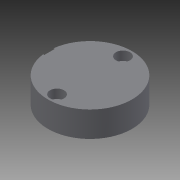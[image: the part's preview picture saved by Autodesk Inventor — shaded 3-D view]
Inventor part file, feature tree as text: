
AUTODESK INVENTOR PART (.ipt)
format: ipt  version: 2014 (Build 180170000, 170)  size: 220,160 bytes
history: native  units: in
note: dims shown in document units (in); Inventor stores cm internally (conversion verified against a paired STEP export)
features: other x189, sketch x9, hole x7, revolve x2, thread x1
ambient origin geometry x8: Origin, YZ Plane, XZ Plane, XY Plane, X Axis, Y Axis, Z Axis, Center Point
bodies: Solid1 (feature_tree)
feature tree (208):
  revolve  "Revolution1"  Angle=360.0deg
  revolve  "Revolution2"  [1 undecoded]
  thread  "Thread1"  [1 undecoded]
  hole  "Hole1"  [1 undecoded]
  hole  "Hole2"  [1 undecoded]
  hole  "Hole3"  [1 undecoded]
  hole  "Hole4"  [1 undecoded]
  hole  "Hole5"  [1 undecoded]
  hole  "Hole6"  [1 undecoded]
  hole  "Hole7"  [1 undecoded]
  other  "a1_XY"
  other  "a1_YZ"
  other  "a1_ZX"
  other  "a1_X"
  other  "a1_Y"
  other  "a1_Z"
  other  "a1_Center"
  other  "a2_XY"
  other  "a2_YZ"
  other  "a2_ZX"
  other  "a2_X"
  other  "a2_Y"
  other  "a2_Z"
  other  "a2_Center"
  other  "ar3_XY"
  other  "ar3_YZ"
  other  "ar3_ZX"
  other  "ar3_X"
  other  "ar3_Y"
  other  "ar3_Z"
  other  "ar3_Center"
  other  "ar4_XY"
  other  "ar4_YZ"
  other  "ar4_ZX"
  other  "ar4_X"
  other  "ar4_Y"
  other  "ar4_Z"
  other  "ar4_Center"
  other  "ar5_XY"
  other  "ar5_YZ"
  other  "ar5_ZX"
  other  "ar5_X"
  other  "ar5_Y"
  other  "ar5_Z"
  other  "ar5_Center"
  other  "ar6_XY"
  other  "ar6_YZ"
  other  "ar6_ZX"
  other  "ar6_X"
  other  "ar6_Y"
  other  "ar6_Z"
  other  "ar6_Center"
  other  "b1_XY"
  other  "b1_YZ"
  other  "b1_ZX"
  other  "b1_X"
  other  "b1_Y"
  other  "b1_Z"
  other  "b1_Center"
  other  "c1_XY"
  other  "c1_YZ"
  other  "c1_ZX"
  other  "c1_X"
  other  "c1_Y"
  other  "c1_Z"
  other  "c1_Center"
  other  "c2_XY"
  other  "c2_YZ"
  other  "c2_ZX"
  other  "c2_X"
  other  "c2_Y"
  other  "c2_Z"
  other  "c2_Center"
  other  "d1_XY"
  other  "d1_YZ"
  other  "d1_ZX"
  other  "d1_X"
  other  "d1_Y"
  other  "d1_Z"
  other  "d1_Center"
  other  "d2_XY"
  other  "d2_YZ"
  other  "d2_ZX"
  other  "d2_X"
  other  "d2_Y"
  other  "d2_Z"
  other  "d2_Center"
  other  "j_XY"
  other  "j_YZ"
  other  "j_ZX"
  other  "j_X"
  other  "j_Y"
  other  "j_Z"
  other  "j_Center"
  other  "k1_XY"
  other  "k1_YZ"
  other  "k1_ZX"
  other  "k1_X"
  other  "k1_Y"
  other  "k1_Z"
  other  "k1_Center"
  other  "k2_XY"
  other  "k2_YZ"
  other  "k2_ZX"
  other  "k2_X"
  other  "k2_Y"
  other  "k2_Z"
  other  "k2_Center"
  other  "l1_XY"
  other  "l1_YZ"
  other  "l1_ZX"
  other  "l1_X"
  other  "l1_Y"
  other  "l1_Z"
  other  "l1_Center"
  other  "l2_XY"
  other  "l2_YZ"
  other  "l2_ZX"
  other  "l2_X"
  other  "l2_Y"
  other  "l2_Z"
  other  "l2_Center"
  other  "rg_XY"
  other  "rg_YZ"
  other  "rg_ZX"
  other  "rg_X"
  other  "rg_Y"
  other  "rg_Z"
  other  "rg_Center"
  other  "rh_XY"
  other  "rh_YZ"
  other  "rh_ZX"
  other  "rh_X"
  other  "rh_Y"
  other  "rh_Z"
  other  "rh_Center"
  other  "to_dummy_XY"
  other  "to_dummy_YZ"
  other  "to_dummy_ZX"
  other  "to_dummy_X"
  other  "to_dummy_Y"
  other  "to_dummy_Z"
  other  "to_dummy_Center"
  other  "to_nut_XY"
  other  "to_nut_YZ"
  other  "to_nut_ZX"
  other  "to_nut_X"
  other  "to_nut_Y"
  other  "to_nut_Z"
  other  "to_nut_Center"
  other  "to_rod_XY"
  other  "to_rod_YZ"
  other  "to_rod_ZX"
  other  "to_rod_X"
  other  "to_rod_Y"
  other  "to_rod_Z"
  other  "to_rod_Center"
  other  "to_tube_XY"
  other  "to_tube_YZ"
  other  "to_tube_ZX"
  other  "to_tube_X"
  other  "to_tube_Y"
  other  "to_tube_Z"
  other  "to_tube_Center"
  other  "to_wiper_XY"
  other  "to_wiper_YZ"
  other  "to_wiper_ZX"
  other  "to_wiper_X"
  other  "to_wiper_Y"
  other  "to_wiper_Z"
  other  "to_wiper_Center"
  other  "track1_XY"
  other  "track1_YZ"
  other  "track1_ZX"
  other  "track1_X"
  other  "track1_Y"
  other  "track1_Z"
  other  "track1_Center"
  other  "track2_XY"
  other  "track2_YZ"
  other  "track2_ZX"
  other  "track2_X"
  other  "track2_Y"
  other  "track2_Z"
  other  "track2_Center"
  other  "track3_XY"
  other  "track3_YZ"
  other  "track3_ZX"
  other  "track3_X"
  other  "track3_Y"
  other  "track3_Z"
  other  "track3_Center"
  other  "track4_XY"
  other  "track4_YZ"
  other  "track4_ZX"
  other  "track4_X"
  other  "track4_Y"
  other  "track4_Z"
  other  "track4_Center"
  sketch  "Sketch_1"  dims[d0=360.0deg d1=360.0deg]
  sketch  "Sketch_37"  dims[d46=0.12in d47=0.75in d48=0.375in d49=0.25in d50=0.5635in d51=0.1in d52=0.0in]
  sketch  "Sketch3"  dims[d2=0.2in d3=0.06in]
  sketch  "Sketch4"  dims[d4=0.61in d5=0.75in d6=0.375in d7=0.25in d8=0.5635in d9=0.1in d10=0.0in]
  sketch  "Sketch5"  dims[d11=0.12in d12=0.75in d13=0.188in d14=0.12in d15=0.5635in d16=0.34in d17=0.0in]
  sketch  "Sketch6"  dims[d18=0.12in d19=0.75in d20=0.188in d21=0.12in d22=0.5635in d23=0.34in d24=0.0in]
  sketch  "Sketch7"  dims[d25=0.12in d26=0.75in d27=0.375in d28=0.25in d29=0.5635in d30=0.1in d31=0.0in]
  sketch  "Sketch8"  dims[d32=0.12in d33=0.75in d34=0.375in d35=0.25in d36=0.5635in d37=0.1in d38=0.0in]
  sketch  "Sketch9"  dims[d39=0.12in d40=0.75in d41=0.375in d42=0.25in d43=0.5635in d44=0.1in d45=0.0in]
note: 9 required parameter values undecoded (feature->parameter linkage not recoverable at this tier; creation-order binding heuristic only, values carry confidence <= 0.55)
